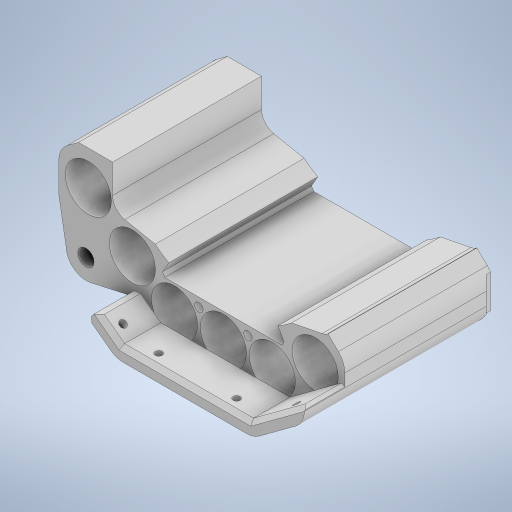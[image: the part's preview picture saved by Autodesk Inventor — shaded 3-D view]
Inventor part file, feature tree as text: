
AUTODESK INVENTOR PART (.ipt)
format: ipt  version: 2023.4 (Build 274418000, 418)  size: 591,360 bytes
history: native  units: mm
features: extrude x13, sketch x13, chamfer x5, thicken_offset x2, projected_geometry x2, fillet x1
ambient origin geometry x8: Origin, YZ Plane, XZ Plane, XY Plane, X Axis, Y Axis, Z Axis, Center Point
bodies: Solid1 (feature_tree)
feature tree (36):
  extrude  "Extrusion1"  Depth=21.7mm
  thicken_offset  "Thicken1"
  extrude  "Extrusion2"  Depth=21.7mm
  extrude  "Extrusion3"  Depth=21.7mm
  chamfer  "Chamfer1"  Distance=0.1mm
  extrude  "Extrusion4"  Depth=54.889727mm
  chamfer  "Chamfer2"  Distance=12.0mm
  extrude  "Extrusion5"  Depth=2.0mm
  chamfer  "Chamfer3"  Distance=23.0mm
  chamfer  "Chamfer4"  [1 undecoded]
  extrude  "Extrusion6"  Depth=2.0mm
  extrude  "Extrusion7"  Depth=2.0mm
  extrude  "Extrusion8"  Depth=2.0mm
  extrude  "Extrusion9"  Depth=2.0mm
  extrude  "Extrusion10"  Depth=2.0mm
  extrude  "Extrusion11"  Depth=2.0mm
  fillet  "Fillet1"  Radius=2.0mm
  chamfer  "Chamfer5"  Distance=5.9mm
  thicken_offset  "Thicken2"
  extrude  "Extrusion12"  Depth=2.0mm
  extrude  "Extrusion13"  Depth=2.0mm
  sketch  "Sketch1"  dims[d0=70.0mm d1=0.0mm d2=21.7mm]
  sketch  "Sketch2"  dims[d3=21.7mm d4=21.7mm]
  projected_geometry  "Projected Loop1"
  sketch  "Sketch3"  dims[d5=21.7mm d6=21.7mm]
  sketch  "Sketch4"  dims[d7=21.7mm d10=0.1mm d11=0.3mm]
  projected_geometry  "Projected Loop2"
  sketch  "Sketch5"  dims[d12=96.0mm d13=54.889727mm]
  sketch  "Sketch6"  dims[d14=54.889727mm]
  sketch  "Sketch7"  dims[d15=60.0mm]
  sketch  "Sketch8"  dims[d16=60.0mm]
  sketch  "Sketch9"  dims[d17=7.0mm]
  sketch  "Sketch10"  dims[d18=7.0mm]
  sketch  "Sketch11"  dims[d19=51.0mm]
  sketch  "Sketch13"  dims[d20=51.0mm]
  sketch  "Sketch15"  dims[d21=12.0mm d22=12.0mm d23=12.0mm d24=23.0mm d25=0.0mm d26=23.0mm d28=102.0mm d29=51.0mm d30=1.5mm d32=1.5mm d33=1.5mm d34=2.0mm d35=0.0mm d36=5.9mm d37=5.9mm d38=38.0mm d39=38.0mm d40=11.5mm d41=11.5mm d42=15.0mm d43=0.0mm d44=5.9mm d45=26.5mm d46=6.0mm d47=1.5mm d48=2.0mm d49=45.0deg d50=1.5mm d51=1.5mm d52=19.0mm d53=0.0mm d54=0.5mm d55=2.0mm d56=45.0deg d57=15.0mm d58=0.0mm d59=11.5mm d60=2.0mm d61=45.0deg d62=5.3mm d63=2.0mm d64=45.0deg d65=6.0mm d66=6.0mm d67=6.0mm d68=3.3mm d69=6.0mm d70=6.0mm d71=0.0mm d72=0.0mm d73=6.0mm d74=3.3mm d75=3.3mm d76=6.0mm d77=12.0mm d78=12.0mm d79=0.0mm d80=0.0mm d81=3.3mm d82=12.0mm d83=6.0mm d84=0.0mm d85=0.0mm d86=5.3mm d87=3.0mm d88=0.0mm d89=5.3mm d90=5.3mm d91=3.0mm d92=0.0mm d93=5.3mm d94=3.0mm d95=0.0mm d96=10.0mm d97=2.0mm d98=2.0mm d99=45.0deg d101=0.25mm d102=0.25mm d103=3.0mm d104=0.0mm d105=4.0mm d106=4.0mm d107=0.0mm d108=0.0mm]
note: 1 required parameter value undecoded (feature->parameter linkage not recoverable at this tier; creation-order binding heuristic only, values carry confidence <= 0.55)
